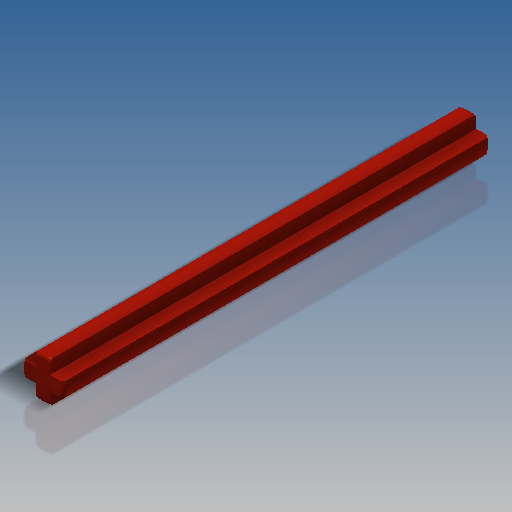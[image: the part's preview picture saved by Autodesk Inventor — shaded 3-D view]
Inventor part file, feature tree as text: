
AUTODESK INVENTOR PART (.ipt)
format: ipt  version: 2019.4 (Build 234330000, 330)  size: 175,104 bytes
history: native  units: in
note: dims shown in document units (in); Inventor stores cm internally (conversion verified against a paired STEP export)
features: extrude x1, fillet x1, sketch x1
ambient origin geometry x8: Origin, YZ Plane, XZ Plane, XY Plane, X Axis, Y Axis, Z Axis, Center Point
bodies: Solid1 (feature_tree)
feature tree (3):
  extrude  "Extrusion1"  Depth=0.0157in
  fillet  "Fillet1"  Radius=1.8898in
  sketch  "Sketch1"  dims[d0=0.189in d1=0.063in d2=1.8898in d3=0.0in d4=0.0157in d5=0.0in d6=0.0in]
